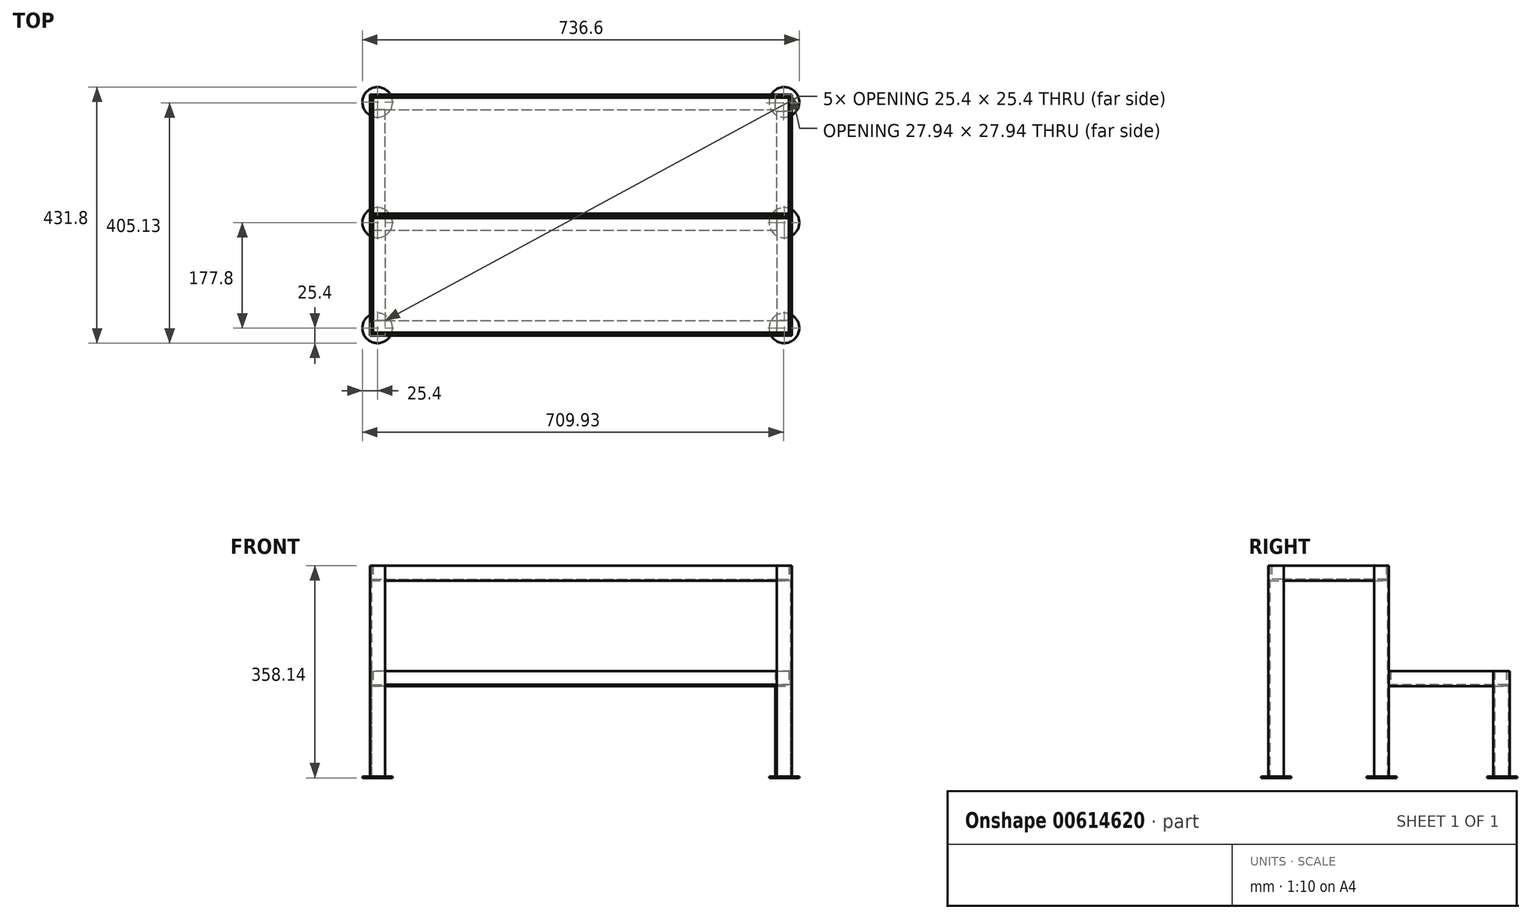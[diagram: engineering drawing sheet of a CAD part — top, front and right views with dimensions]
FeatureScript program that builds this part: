
annotation { "Feature Type Name" : "Feature", "Feature Type Description" : "" }
export const myFeature = defineFeature(function(context is Context, id is Id, definition is map)
    precondition{}
    {
        {
            var Q0;
            Q0=qCreatedBy(makeId("Top.planeOp"),FACE);
            var sketch = newSketch(context, id + "F0", { "sketchPlane" : qUnion([Q0])});
            skLineSegment(sketch, "E0", {"start": v(0, 0) * mm, "end": v(0, 25.4) * mm});
            skLineSegment(sketch, "E1", {"start": v(0, 25.4) * mm, "end": v(25.4, 25.4) * mm});
            skLineSegment(sketch, "E2", {"start": v(25.4, 25.4) * mm, "end": v(25.4, 22.86) * mm});
            skLineSegment(sketch, "E3", {"start": v(25.4, 22.86) * mm, "end": v(2.54, 22.86) * mm});
            skLineSegment(sketch, "E4", {"start": v(2.54, 22.86) * mm, "end": v(2.54, 0) * mm});
            skLineSegment(sketch, "E5", {"start": v(2.54, 0) * mm, "end": v(0, 0) * mm});
            skLineSegment(sketch, "E6", {"start": v(685.8, 25.4) * mm, "end": v(711.2, 25.4) * mm});
            skLineSegment(sketch, "E7", {"start": v(711.2, 25.4) * mm, "end": v(711.2, 0) * mm});
            skLineSegment(sketch, "E8", {"start": v(711.2, 0) * mm, "end": v(708.66, 0) * mm});
            skLineSegment(sketch, "E9", {"start": v(708.66, 0) * mm, "end": v(708.66, 22.86) * mm});
            skLineSegment(sketch, "E10", {"start": v(708.66, 22.86) * mm, "end": v(685.8, 22.86) * mm});
            skLineSegment(sketch, "E11", {"start": v(685.8, 22.86) * mm, "end": v(685.8, 25.4) * mm});
            skLineSegment(sketch, "E12", {"start": v(0, -152.4) * mm, "end": v(0, -177.8) * mm});
            skLineSegment(sketch, "E13", {"start": v(0, -177.8) * mm, "end": v(25.4, -177.8) * mm});
            skLineSegment(sketch, "E14", {"start": v(25.4, -177.8) * mm, "end": v(25.4, -175.26) * mm});
            skLineSegment(sketch, "E15", {"start": v(25.4, -175.26) * mm, "end": v(2.54, -175.26) * mm});
            skLineSegment(sketch, "E16", {"start": v(2.54, -175.26) * mm, "end": v(2.54, -152.4) * mm});
            skLineSegment(sketch, "E17", {"start": v(2.54, -152.4) * mm, "end": v(0, -152.4) * mm});
            skLineSegment(sketch, "E18", {"start": v(711.2, -177.8) * mm, "end": v(711.2, -152.4) * mm});
            skLineSegment(sketch, "E19", {"start": v(711.2, -152.4) * mm, "end": v(708.66, -152.4) * mm});
            skLineSegment(sketch, "E20", {"start": v(708.66, -152.4) * mm, "end": v(708.66, -175.26) * mm});
            skLineSegment(sketch, "E21", {"start": v(708.66, -175.26) * mm, "end": v(685.8, -175.26) * mm});
            skLineSegment(sketch, "E22", {"start": v(685.8, -175.26) * mm, "end": v(685.8, -177.8) * mm});
            skLineSegment(sketch, "E23", {"start": v(685.8, -177.8) * mm, "end": v(711.2, -177.8) * mm});
            skLineSegment(sketch, "E24", {"start": v(0, 228.6) * mm, "end": v(25.4, 228.6) * mm});
            skLineSegment(sketch, "E25", {"start": v(25.4, 228.6) * mm, "end": v(25.4, 226.06) * mm});
            skLineSegment(sketch, "E26", {"start": v(25.4, 226.06) * mm, "end": v(2.54, 226.06) * mm});
            skLineSegment(sketch, "E27", {"start": v(2.54, 226.06) * mm, "end": v(2.54, 203.2) * mm});
            skLineSegment(sketch, "E28", {"start": v(2.54, 203.2) * mm, "end": v(0, 203.2) * mm});
            skLineSegment(sketch, "E29", {"start": v(0, 203.2) * mm, "end": v(0, 228.6) * mm});
            skLineSegment(sketch, "E30", {"start": v(683.26, 226.06) * mm, "end": v(708.66, 226.06) * mm});
            skLineSegment(sketch, "E31", {"start": v(708.66, 226.06) * mm, "end": v(708.66, 200.66) * mm});
            skLineSegment(sketch, "E32", {"start": v(711.2, 200.66) * mm, "end": v(708.66, 200.66) * mm});
            skLineSegment(sketch, "E33", {"start": v(711.2, 200.66) * mm, "end": v(711.2, 228.6) * mm});
            skLineSegment(sketch, "E34", {"start": v(711.2, 228.6) * mm, "end": v(683.26, 228.6) * mm});
            skLineSegment(sketch, "E35", {"start": v(683.26, 226.06) * mm, "end": v(683.26, 228.6) * mm});
            skSolve(sketch);
        }
        {
            var Q0;
            Q0=makeQuery(id+"F0.imprint","IMPRINT",FACE,{"disambiguationData":[TD([[makeQuery(id+"F0.imprint","IMPRINT",EDGE,{"derivedFrom":sQuery(id+"F0.wireOp",EDGE,"E12")}),1.0]])]});
            var Q1;
            Q1=makeQuery(id+"F0.imprint","IMPRINT",FACE,{"disambiguationData":[TD([[makeQuery(id+"F0.imprint","IMPRINT",EDGE,{"derivedFrom":sQuery(id+"F0.wireOp",EDGE,"E6")}),-1.0]])]});
            var Q2;
            Q2=makeQuery(id+"F0.imprint","IMPRINT",FACE,{"disambiguationData":[TD([[makeQuery(id+"F0.imprint","IMPRINT",EDGE,{"derivedFrom":sQuery(id+"F0.wireOp",EDGE,"E18")}),1.0]])]});
            var Q3;
            Q3=makeQuery(id+"F0.imprint","IMPRINT",FACE,{"disambiguationData":[TD([[makeQuery(id+"F0.imprint","IMPRINT",EDGE,{"derivedFrom":sQuery(id+"F0.wireOp",EDGE,"E0")}),-1.0]])]});
            extrude(context, id + "F1", {"entities" : qUnion([Q0, Q1, Q2, Q3]), "depth" : 355.6 * mm, "offsetDistance" : 25.4 * mm});
        }
        {
            var Q0;
            Q0=makeQuery(id+"F0.imprint","IMPRINT",FACE,{"disambiguationData":[TD([[makeQuery(id+"F0.imprint","IMPRINT",EDGE,{"derivedFrom":sQuery(id+"F0.wireOp",EDGE,"E24")}),-1.0]])]});
            var Q1;
            Q1=makeQuery(id+"F0.imprint","IMPRINT",FACE,{"disambiguationData":[TD([[makeQuery(id+"F0.imprint","IMPRINT",EDGE,{"derivedFrom":sQuery(id+"F0.wireOp",EDGE,"E30")}),1.0]])]});
            extrude(context, id + "F2", {"entities" : qUnion([Q0, Q1]), "depth" : 177.8 * mm, "offsetDistance" : 25.4 * mm});
        }
        {
            var Q0;
            Q0=makeQuery(id+"F1.opExtrude","SWEPT_FACE",FACE,{"disambiguationData":[OSD([sQuery(id+"F0.wireOp",EDGE,"E11")])]});
            var sketch = newSketch(context, id + "F3", { "sketchPlane" : qUnion([Q0])});
            skLineSegment(sketch, "E36", {"start": v(-25.4, 355.6) * mm, "end": v(-25.4, 330.2) * mm});
            skLineSegment(sketch, "E37", {"start": v(-25.4, 330.2) * mm, "end": v(0, 330.2) * mm});
            skLineSegment(sketch, "E38", {"start": v(0, 330.2) * mm, "end": v(0, 332.74) * mm});
            skLineSegment(sketch, "E39", {"start": v(0, 332.74) * mm, "end": v(-22.86, 332.74) * mm});
            skLineSegment(sketch, "E40", {"start": v(-22.86, 332.74) * mm, "end": v(-22.86, 355.6) * mm});
            skLineSegment(sketch, "E41", {"start": v(-22.86, 355.6) * mm, "end": v(-25.4, 355.6) * mm});
            skSolve(sketch);
        }
        {
            var Q0;
            {var subQ1=sQuery(id+"F3.wireOp",EDGE,"E36");Q0=makeQuery(id+"F3.imprint","IMPRINT",FACE,{"disambiguationData":[TD([[makeQuery(id+"F3.imprint","IMPRINT",EDGE,{"derivedFrom":subQ1}),1.0]])]});}
            var Q1;
            {var subQ0=sQuery(id+"F3.wireOp",EDGE,"E38");Q1=makeQuery(id+"F3.imprint","IMPRINT",FACE,{"disambiguationData":[TD([[makeQuery(id+"F3.imprint","IMPRINT",EDGE,{"derivedFrom":subQ0}),1.0]])]});}
            extrude(context, id + "F4", {"entities" : qUnion([Q0, Q1]), "endBound" : BoundingType.UP_TO_NEXT, "depth" : 25.4 * mm, "offsetDistance" : 25.4 * mm});
        }
        {
            var Q0;
            Q0=makeQuery(id+"F1.opExtrude","SWEPT_FACE",FACE,{"disambiguationData":[OSD([sQuery(id+"F0.wireOp",EDGE,"E22")])]});
            var sketch = newSketch(context, id + "F5", { "sketchPlane" : qUnion([Q0])});
            skLineSegment(sketch, "E42", {"start": v(177.8, 355.6) * mm, "end": v(177.8, 330.2) * mm});
            skLineSegment(sketch, "E43", {"start": v(177.8, 330.2) * mm, "end": v(152.4, 330.2) * mm});
            skLineSegment(sketch, "E44", {"start": v(152.4, 330.2) * mm, "end": v(152.4, 332.74) * mm});
            skLineSegment(sketch, "E45", {"start": v(152.4, 332.74) * mm, "end": v(175.26, 332.74) * mm});
            skLineSegment(sketch, "E46", {"start": v(175.26, 332.74) * mm, "end": v(175.26, 355.6) * mm});
            skLineSegment(sketch, "E47", {"start": v(175.26, 355.6) * mm, "end": v(177.8, 355.6) * mm});
            skSolve(sketch);
        }
        {
            var Q0;
            Q0 = qSketchRegion(id + "F5", true);
            extrude(context, id + "F6", {"entities" : qUnion([Q0]), "endBound" : BoundingType.UP_TO_NEXT, "depth" : 25.4 * mm, "offsetDistance" : 25.4 * mm});
        }
        {
            var Q0;
            Q0=makeQuery(id+"F1.opExtrude","SWEPT_FACE",FACE,{"disambiguationData":[OSD([sQuery(id+"F0.wireOp",EDGE,"E17")])]});
            var sketch = newSketch(context, id + "F7", { "sketchPlane" : qUnion([Q0])});
            skLineSegment(sketch, "E48", {"start": v(0, 355.6) * mm, "end": v(0, 330.2) * mm});
            skLineSegment(sketch, "E49", {"start": v(0, 330.2) * mm, "end": v(-25.4, 330.2) * mm});
            skLineSegment(sketch, "E50", {"start": v(-25.4, 330.2) * mm, "end": v(-25.4, 332.74) * mm});
            skLineSegment(sketch, "E51", {"start": v(-25.4, 332.74) * mm, "end": v(-2.54, 332.74) * mm});
            skLineSegment(sketch, "E52", {"start": v(-2.54, 332.74) * mm, "end": v(-2.54, 355.6) * mm});
            skLineSegment(sketch, "E53", {"start": v(-2.54, 355.6) * mm, "end": v(0, 355.6) * mm});
            skSolve(sketch);
        }
        {
            var Q0;
            Q0 = qSketchRegion(id + "F7", true);
            var Q1;
            Q1=makeQuery(id+"F1.opExtrude","SWEPT_BODY",BODY,{"disambiguationData":[OSD([sQuery(id+"F0.wireOp",EDGE,"E0"),sQuery(id+"F0.wireOp",EDGE,"E1"),sQuery(id+"F0.wireOp",EDGE,"E2"),sQuery(id+"F0.wireOp",EDGE,"E3"),sQuery(id+"F0.wireOp",EDGE,"E4"),sQuery(id+"F0.wireOp",EDGE,"E5")])]});
            extrude(context, id + "F8", {"entities" : qUnion([Q0]), "endBound" : BoundingType.UP_TO_BODY, "depth" : 25.4 * mm, "endBoundEntityBody" : qUnion([Q1]), "offsetDistance" : 25.4 * mm});
        }
        {
            var Q0;
            Q0=makeQuery(id+"F1.opExtrude","SWEPT_FACE",FACE,{"disambiguationData":[OSD([sQuery(id+"F0.wireOp",EDGE,"E19")])]});
            var sketch = newSketch(context, id + "F9", { "sketchPlane" : qUnion([Q0])});
            skLineSegment(sketch, "E54", {"start": v(-711.2, 355.6) * mm, "end": v(-708.66, 355.6) * mm});
            skLineSegment(sketch, "E55", {"start": v(-708.66, 355.6) * mm, "end": v(-708.66, 332.74) * mm});
            skLineSegment(sketch, "E56", {"start": v(-708.66, 332.74) * mm, "end": v(-685.8, 332.74) * mm});
            skLineSegment(sketch, "E57", {"start": v(-685.8, 332.74) * mm, "end": v(-685.8, 330.2) * mm});
            skLineSegment(sketch, "E58", {"start": v(-685.8, 330.2) * mm, "end": v(-711.2, 330.2) * mm});
            skLineSegment(sketch, "E59", {"start": v(-711.2, 330.2) * mm, "end": v(-711.2, 355.6) * mm});
            skSolve(sketch);
        }
        {
            var Q0;
            Q0 = qSketchRegion(id + "F9", true);
            extrude(context, id + "F10", {"entities" : qUnion([Q0]), "endBound" : BoundingType.UP_TO_NEXT, "depth" : 25.4 * mm, "offsetDistance" : 25.4 * mm});
        }
        {
            var Q0;
            Q0=makeQuery(id+"F2.opExtrude","SWEPT_FACE",FACE,{"disambiguationData":[OSD([sQuery(id+"F0.wireOp",EDGE,"E35")])]});
            var sketch = newSketch(context, id + "F11", { "sketchPlane" : qUnion([Q0])});
            skLineSegment(sketch, "E60", {"start": v(-228.6, 177.8) * mm, "end": v(-228.6, 152.4) * mm});
            skLineSegment(sketch, "E61", {"start": v(-228.6, 152.4) * mm, "end": v(-203.2, 152.4) * mm});
            skLineSegment(sketch, "E62", {"start": v(-203.2, 152.4) * mm, "end": v(-203.2, 154.94) * mm});
            skLineSegment(sketch, "E63", {"start": v(-203.2, 154.94) * mm, "end": v(-226.06, 154.94) * mm});
            skLineSegment(sketch, "E64", {"start": v(-226.06, 154.94) * mm, "end": v(-226.06, 177.8) * mm});
            skLineSegment(sketch, "E65", {"start": v(-226.06, 177.8) * mm, "end": v(-228.6, 177.8) * mm});
            skSolve(sketch);
        }
        {
            var Q0;
            Q0 = qSketchRegion(id + "F11", true);
            extrude(context, id + "F12", {"entities" : qUnion([Q0]), "endBound" : BoundingType.UP_TO_NEXT, "depth" : 25.4 * mm, "offsetDistance" : 25.4 * mm});
        }
        {
            var Q0;
            Q0=makeQuery(id+"F2.opExtrude","SWEPT_FACE",FACE,{"disambiguationData":[OSD([sQuery(id+"F0.wireOp",EDGE,"E32")])]});
            var sketch = newSketch(context, id + "F13", { "sketchPlane" : qUnion([Q0])});
            skLineSegment(sketch, "E66", {"start": v(711.2, 177.8) * mm, "end": v(711.2, 152.4) * mm});
            skLineSegment(sketch, "E67", {"start": v(711.2, 152.4) * mm, "end": v(685.8, 152.4) * mm});
            skLineSegment(sketch, "E68", {"start": v(685.8, 152.4) * mm, "end": v(685.8, 154.94) * mm});
            skLineSegment(sketch, "E69", {"start": v(685.8, 154.94) * mm, "end": v(708.66, 154.94) * mm});
            skLineSegment(sketch, "E70", {"start": v(708.66, 154.94) * mm, "end": v(708.66, 177.8) * mm});
            skLineSegment(sketch, "E71", {"start": v(708.66, 177.8) * mm, "end": v(711.2, 177.8) * mm});
            skSolve(sketch);
        }
        {
            var Q0;
            Q0 = qSketchRegion(id + "F13", true);
            extrude(context, id + "F14", {"entities" : qUnion([Q0]), "endBound" : BoundingType.UP_TO_NEXT, "depth" : 25.4 * mm, "offsetDistance" : 25.4 * mm});
        }
        {
            var Q0;
            Q0=makeQuery(id+"F2.opExtrude","SWEPT_FACE",FACE,{"disambiguationData":[OSD([sQuery(id+"F0.wireOp",EDGE,"E28")])]});
            var sketch = newSketch(context, id + "F15", { "sketchPlane" : qUnion([Q0])});
            skLineSegment(sketch, "E72", {"start": v(0, 177.8) * mm, "end": v(0, 152.4) * mm});
            skLineSegment(sketch, "E73", {"start": v(0, 152.4) * mm, "end": v(25.4, 152.4) * mm});
            skLineSegment(sketch, "E74", {"start": v(25.4, 152.4) * mm, "end": v(25.4, 154.94) * mm});
            skLineSegment(sketch, "E75", {"start": v(25.4, 154.94) * mm, "end": v(2.54, 154.94) * mm});
            skLineSegment(sketch, "E76", {"start": v(2.54, 154.94) * mm, "end": v(2.54, 177.8) * mm});
            skLineSegment(sketch, "E77", {"start": v(2.54, 177.8) * mm, "end": v(0, 177.8) * mm});
            skSolve(sketch);
        }
        {
            var Q0;
            Q0 = qSketchRegion(id + "F15", true);
            extrude(context, id + "F16", {"entities" : qUnion([Q0]), "endBound" : BoundingType.UP_TO_NEXT, "depth" : 25.4 * mm, "offsetDistance" : 25.4 * mm});
        }
        {
            var Q0;
            Q0=makeQuery(id+"F0.imprint","IMPRINT",FACE,{"disambiguationData":[TD([[makeQuery(id+"F0.imprint","IMPRINT",EDGE,{"derivedFrom":sQuery(id+"F0.wireOp",EDGE,"E30")}),1.0]])]});
            var sketch = newSketch(context, id + "F17", { "sketchPlane" : qUnion([Q0])});
            skCircle(sketch, "E78", {"center": v(698.5, 215.9) * mm, "radius": 25.4 * mm});
            skSolve(sketch);
        }
        {
            var Q0;
            Q0=makeQuery(id+"F0.imprint","IMPRINT",FACE,{"disambiguationData":[TD([[makeQuery(id+"F0.imprint","IMPRINT",EDGE,{"derivedFrom":sQuery(id+"F0.wireOp",EDGE,"E24")}),-1.0]])]});
            var sketch = newSketch(context, id + "F18", { "sketchPlane" : qUnion([Q0])});
            skCircle(sketch, "E79", {"center": v(12.7, 215.9) * mm, "radius": 25.4 * mm});
            skSolve(sketch);
        }
        {
            var Q0;
            Q0=makeQuery(id+"F0.imprint","IMPRINT",FACE,{"disambiguationData":[TD([[makeQuery(id+"F0.imprint","IMPRINT",EDGE,{"derivedFrom":sQuery(id+"F0.wireOp",EDGE,"E12")}),1.0]])]});
            var sketch = newSketch(context, id + "F19", { "sketchPlane" : qUnion([Q0])});
            skCircle(sketch, "E80", {"center": v(12.7, -165.1) * mm, "radius": 25.4 * mm});
            skSolve(sketch);
        }
        {
            var Q0;
            Q0=makeQuery(id+"F0.imprint","IMPRINT",FACE,{"disambiguationData":[TD([[makeQuery(id+"F0.imprint","IMPRINT",EDGE,{"derivedFrom":sQuery(id+"F0.wireOp",EDGE,"E18")}),1.0]])]});
            var sketch = newSketch(context, id + "F20", { "sketchPlane" : qUnion([Q0])});
            skCircle(sketch, "E81", {"center": v(698.5, -165.1) * mm, "radius": 25.4 * mm});
            skSolve(sketch);
        }
        {
            var Q0;
            Q0=makeQuery(id+"F0.imprint","IMPRINT",FACE,{"disambiguationData":[TD([[makeQuery(id+"F0.imprint","IMPRINT",EDGE,{"derivedFrom":sQuery(id+"F0.wireOp",EDGE,"E6")}),-1.0]])]});
            var sketch = newSketch(context, id + "F21", { "sketchPlane" : qUnion([Q0])});
            skCircle(sketch, "E82", {"center": v(698.5, 12.7) * mm, "radius": 25.4 * mm});
            skSolve(sketch);
        }
        {
            var Q0;
            Q0=makeQuery(id+"F0.imprint","IMPRINT",FACE,{"disambiguationData":[TD([[makeQuery(id+"F0.imprint","IMPRINT",EDGE,{"derivedFrom":sQuery(id+"F0.wireOp",EDGE,"E0")}),-1.0]])]});
            var sketch = newSketch(context, id + "F22", { "sketchPlane" : qUnion([Q0])});
            skCircle(sketch, "E83", {"center": v(12.7, 12.7) * mm, "radius": 25.4 * mm});
            skSolve(sketch);
        }
        {
            var Q0;
            Q0=makeQuery(id+"F19.imprint","IMPRINT",FACE,{"disambiguationData":[TD([[makeQuery(id+"F19.imprint","IMPRINT",EDGE,{"derivedFrom":sQuery(id+"F19.wireOp",EDGE,"E80")}),1.0]])]});
            var Q1;
            Q1=makeQuery(id+"F22.imprint","IMPRINT",FACE,{"disambiguationData":[TD([[makeQuery(id+"F22.imprint","IMPRINT",EDGE,{"derivedFrom":sQuery(id+"F22.wireOp",EDGE,"E83")}),1.0]])]});
            var Q2;
            Q2=makeQuery(id+"F18.imprint","IMPRINT",FACE,{"disambiguationData":[TD([[makeQuery(id+"F18.imprint","IMPRINT",EDGE,{"derivedFrom":sQuery(id+"F18.wireOp",EDGE,"E79")}),1.0]])]});
            var Q3;
            Q3=makeQuery(id+"F20.imprint","IMPRINT",FACE,{"disambiguationData":[TD([[makeQuery(id+"F20.imprint","IMPRINT",EDGE,{"derivedFrom":sQuery(id+"F20.wireOp",EDGE,"E81")}),1.0]])]});
            var Q4;
            Q4=makeQuery(id+"F21.imprint","IMPRINT",FACE,{"disambiguationData":[TD([[makeQuery(id+"F21.imprint","IMPRINT",EDGE,{"derivedFrom":sQuery(id+"F21.wireOp",EDGE,"E82")}),1.0]])]});
            var Q5;
            Q5=makeQuery(id+"F17.imprint","IMPRINT",FACE,{"disambiguationData":[TD([[makeQuery(id+"F17.imprint","IMPRINT",EDGE,{"derivedFrom":sQuery(id+"F17.wireOp",EDGE,"E78")}),1.0]])]});
            extrude(context, id + "F23", {"entities" : qUnion([Q0, Q1, Q2, Q3, Q4, Q5]), "oppositeDirection" : true, "depth" : 2.54 * mm, "offsetDistance" : 25.4 * mm});
        }
        {
            var Q0;
            Q0=makeQuery(id+"F10.opExtrude","SWEPT_FACE",FACE,{"disambiguationData":[OSD([sQuery(id+"F9.wireOp",EDGE,"E56")])]});
            var sketch = newSketch(context, id + "F24", { "sketchPlane" : qUnion([Q0])});
            skPoint(sketch, "E84.oppositeSnap0", {"position": v(706.12, -76.2) * mm});
            skLineSegment(sketch, "E84.bottom", {"start": v(5.08, 20.32) * mm, "end": v(706.12, 20.32) * mm});
            skLineSegment(sketch, "E84.top", {"start": v(5.08, -172.72) * mm, "end": v(706.12, -172.72) * mm});
            skLineSegment(sketch, "E84.left", {"start": v(5.08, 20.32) * mm, "end": v(5.08, -172.72) * mm});
            skLineSegment(sketch, "E84.right", {"start": v(706.12, 20.32) * mm, "end": v(706.12, -172.72) * mm});
            skSolve(sketch);
        }
        {
            var Q0;
            Q0 = qSketchRegion(id + "F24", true);
            extrude(context, id + "F25", {"entities" : qUnion([Q0]), "depth" : 22.86 * mm, "offsetDistance" : 25.4 * mm});
        }
        {
            var Q0;
            Q0=makeQuery(id+"F14.opExtrude","SWEPT_FACE",FACE,{"disambiguationData":[OSD([sQuery(id+"F13.wireOp",EDGE,"E69")])]});
            var sketch = newSketch(context, id + "F26", { "sketchPlane" : qUnion([Q0])});
            skLineSegment(sketch, "E85.bottom", {"start": v(5.08, 223.52) * mm, "end": v(706.12, 223.52) * mm});
            skLineSegment(sketch, "E85.top", {"start": v(5.08, 27.94) * mm, "end": v(706.12, 27.94) * mm});
            skLineSegment(sketch, "E85.left", {"start": v(5.08, 223.52) * mm, "end": v(5.08, 27.94) * mm});
            skLineSegment(sketch, "E85.right", {"start": v(706.12, 223.52) * mm, "end": v(706.12, 27.94) * mm});
            skSolve(sketch);
        }
        {
            var Q0;
            Q0 = qSketchRegion(id + "F26", true);
            extrude(context, id + "F27", {"entities" : qUnion([Q0]), "depth" : 22.86 * mm, "offsetDistance" : 25.4 * mm});
        }
    });
